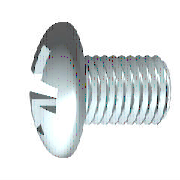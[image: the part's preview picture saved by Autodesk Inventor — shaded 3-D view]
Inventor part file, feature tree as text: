
AUTODESK INVENTOR PART (.ipt)
format: ipt  version: 2020 (Build 240168000, 168)  size: 280,064 bytes
history: native  units: mm (DEFAULTED — no unit token found)
features: other x2, plane x2, extrude x1
ambient origin geometry x7: Origin, YZ Plane, XZ Plane, X Axis, Y Axis, Z Axis, Center Point
bodies: Solid1 (feature_tree)
feature tree (5):
  other  "Базовый элемент"
  plane  "Work Plane1"
  extrude  "Паз"  Depth=3.0mm
  other  "Вырез"
  plane  "Work Plane3"
